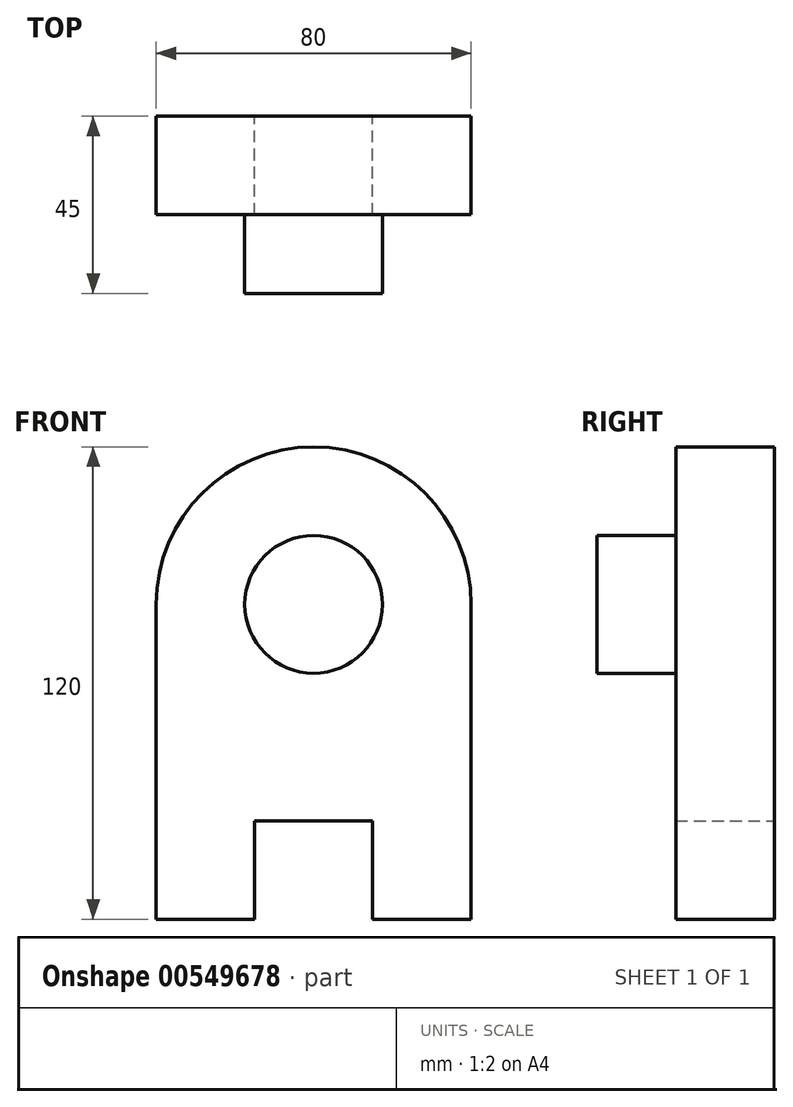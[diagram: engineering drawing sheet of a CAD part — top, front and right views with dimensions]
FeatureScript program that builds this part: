
annotation { "Feature Type Name" : "Feature", "Feature Type Description" : "" }
export const myFeature = defineFeature(function(context is Context, id is Id, definition is map)
    precondition{}
    {
        {
            var Q0;
            Q0=qCreatedBy(makeId("Front.planeOp"),FACE);
            var sketch = newSketch(context, id + "F0", { "sketchPlane" : qUnion([Q0])});
            skLineSegment(sketch, "E0.bottom", {"start": v(40, -40) * mm, "end": v(15, -40) * mm});
            skLineSegment(sketch, "E0.left", {"start": v(40, -40) * mm, "end": v(40, 40) * mm});
            skLineSegment(sketch, "E0.right", {"start": v(-40, -40) * mm, "end": v(-40, 40) * mm});
            skPoint(sketch, "E0.middle", {"position": v(0, 0) * mm});
            skArc(sketch, "E1", {"start": v(40, 40) * mm, "mid": v(0, 80) * mm, "end": v(-40, 40) * mm});
            skLineSegment(sketch, "E2.bottom", {"start": v(-15, -15) * mm, "end": v(15, -15) * mm});
            skLineSegment(sketch, "E2.left", {"start": v(-15, -15) * mm, "end": v(-15, -40) * mm});
            skLineSegment(sketch, "E2.right", {"start": v(15, -15) * mm, "end": v(15, -40) * mm});
            skPoint(sketch, "E2.middle", {"position": v(0, -40) * mm});
            skPoint(sketch, "E3.orphan", {"position": v(-15, -65) * mm});
            skPoint(sketch, "E4.orphan", {"position": v(15, -65) * mm});
            skLineSegment(sketch, "E5.trimOffspring", {"start": v(-15, -40) * mm, "end": v(-40, -40) * mm});
            skSolve(sketch);
        }
        {
            var Q0;
            Q0 = qSketchRegion(id + "F0", true);
            extrude(context, id + "F1", {"entities" : qUnion([Q0]), "depth" : (80 - 30) * mm / 2, "offsetDistance" : 25 * mm});
        }
        {
            var Q0;
            Q0=makeQuery(id+"F1.opExtrude","CAP_FACE",FACE,{"disambiguationData":[OSD([sQuery(id+"F0.wireOp",EDGE,"E0.bottom"),sQuery(id+"F0.wireOp",EDGE,"E0.left"),sQuery(id+"F0.wireOp",EDGE,"E0.right"),sQuery(id+"F0.wireOp",EDGE,"E1"),sQuery(id+"F0.wireOp",EDGE,"E2.bottom"),sQuery(id+"F0.wireOp",EDGE,"E2.left"),sQuery(id+"F0.wireOp",EDGE,"E2.right"),sQuery(id+"F0.wireOp",EDGE,"E5.trimOffspring")])],"isStart":false});
            var sketch = newSketch(context, id + "F2", { "sketchPlane" : qUnion([Q0])});
            skCircle(sketch, "E6", {"center": v(0, 40) * mm, "radius": 17.5 * mm});
            skSolve(sketch);
        }
        {
            var Q0;
            Q0=makeQuery(id+"F2.imprint","IMPRINT",FACE,{"disambiguationData":[TD([[makeQuery(id+"F2.imprint","IMPRINT",EDGE,{"derivedFrom":sQuery(id+"F2.wireOp",EDGE,"E6")}),1.0]])]});
            extrude(context, id + "F3", {"entities" : qUnion([Q0]), "operationType" : NewBodyOperationType.ADD, "depth" : 20 * mm, "offsetDistance" : 25 * mm});
        }
    });
